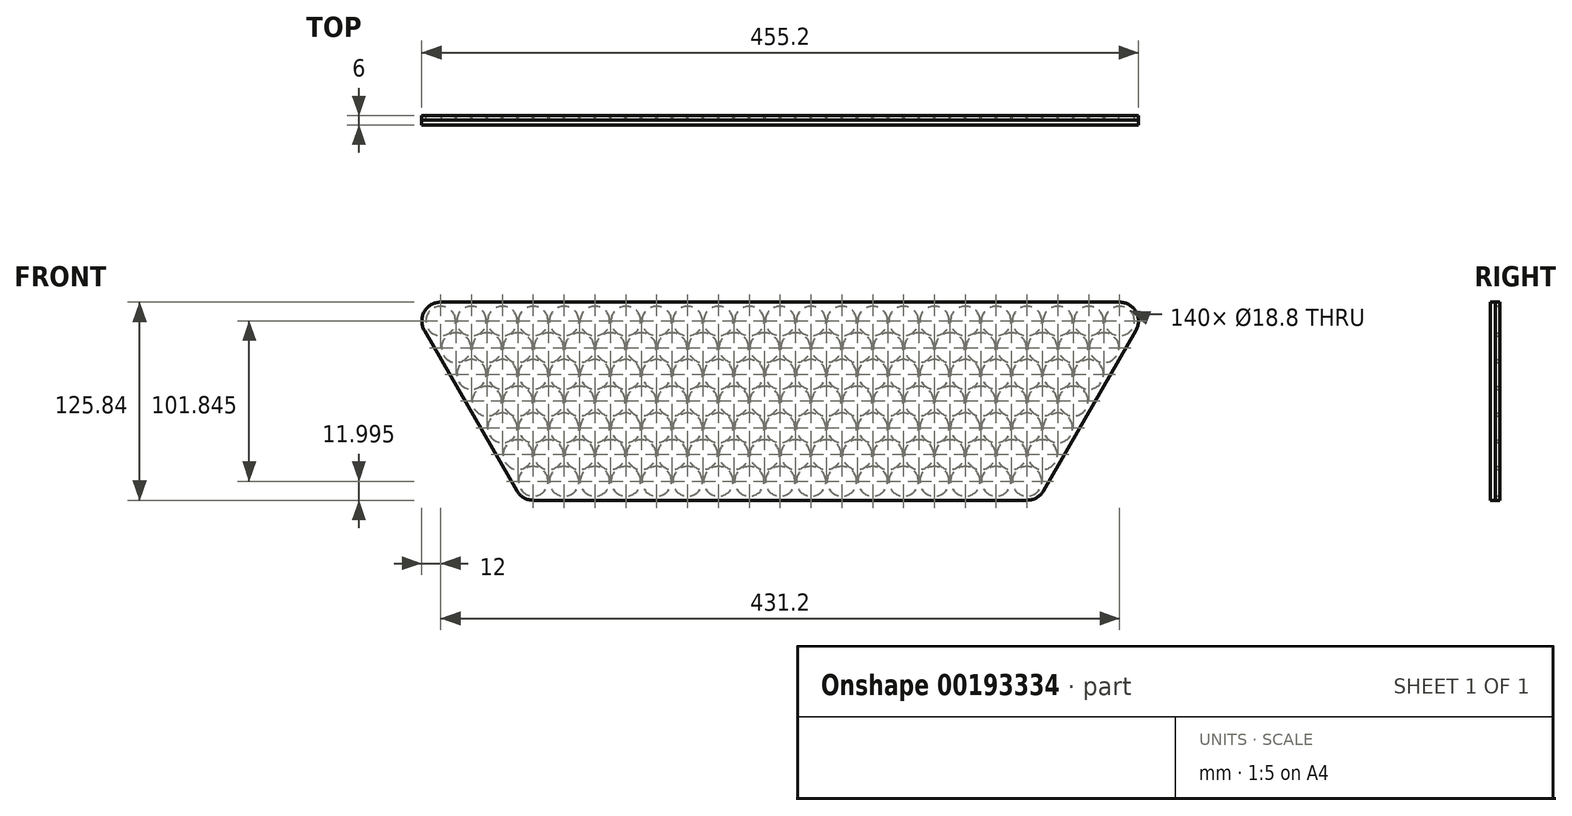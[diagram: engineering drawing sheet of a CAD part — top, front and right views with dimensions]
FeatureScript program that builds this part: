
annotation { "Feature Type Name" : "Feature", "Feature Type Description" : "" }
export const myFeature = defineFeature(function(context is Context, id is Id, definition is map)
    precondition{}
    {
        {
            var Q0;
            Q0=qCreatedBy(makeId("Front.planeOp"),FACE);
            var sketch = newSketch(context, id + "F0", { "sketchPlane" : qUnion([Q0])});
            skLineSegment(sketch, "E0", {"start": v(0, 0) * mm, "end": v(79.44, 0) * mm, "construction": true});
            skLineSegment(sketch, "E1", {"start": v(0, 0) * mm, "end": v(43.4, -75.16) * mm, "construction": true});
            skCircle(sketch, "E2", {"center": v(0, 0) * mm, "radius": 9.4 * mm});
            skCircle(sketch, "E3.1.0.0", {"center": v(19.6, 0) * mm, "radius": 9.4 * mm});
            skCircle(sketch, "E3.2.0.0", {"center": v(39.2, 0) * mm, "radius": 9.4 * mm});
            skCircle(sketch, "E3.3.0.0", {"center": v(58.8, 0) * mm, "radius": 9.4 * mm});
            skCircle(sketch, "E3.4.0.0", {"center": v(78.4, 0) * mm, "radius": 9.4 * mm});
            skCircle(sketch, "E3.5.0.0", {"center": v(98, 0) * mm, "radius": 9.4 * mm});
            skCircle(sketch, "E3.6.0.0", {"center": v(117.6, 0) * mm, "radius": 9.4 * mm});
            skCircle(sketch, "E3.7.0.0", {"center": v(137.2, 0) * mm, "radius": 9.4 * mm});
            skCircle(sketch, "E3.8.0.0", {"center": v(156.8, 0) * mm, "radius": 9.4 * mm});
            skCircle(sketch, "E3.9.0.0", {"center": v(176.4, 0) * mm, "radius": 9.4 * mm});
            skCircle(sketch, "E3.10.0.0", {"center": v(196, 0) * mm, "radius": 9.4 * mm});
            skCircle(sketch, "E3.11.0.0", {"center": v(215.6, 0) * mm, "radius": 9.4 * mm});
            skCircle(sketch, "E3.12.0.0", {"center": v(235.2, 0) * mm, "radius": 9.4 * mm});
            skCircle(sketch, "E3.13.0.0", {"center": v(254.8, 0) * mm, "radius": 9.4 * mm});
            skCircle(sketch, "E3.14.0.0", {"center": v(274.4, 0) * mm, "radius": 9.4 * mm});
            skCircle(sketch, "E3.15.0.0", {"center": v(294, 0) * mm, "radius": 9.4 * mm});
            skCircle(sketch, "E3.16.0.0", {"center": v(313.6, 0) * mm, "radius": 9.4 * mm});
            skCircle(sketch, "E3.17.0.0", {"center": v(333.2, 0) * mm, "radius": 9.4 * mm});
            skCircle(sketch, "E3.18.0.0", {"center": v(352.8, 0) * mm, "radius": 9.4 * mm});
            skCircle(sketch, "E3.19.0.0", {"center": v(372.4, 0) * mm, "radius": 9.4 * mm});
            skLineSegment(sketch, "E3.direction1", {"start": v(0, 0) * mm, "end": v(19.6, 0) * mm, "construction": true});
            skCircle(sketch, "E4.1.0.0", {"center": v(9.8, -16.97) * mm, "radius": 9.4 * mm});
            skCircle(sketch, "E4.2.0.0", {"center": v(19.6, -33.95) * mm, "radius": 9.4 * mm});
            skCircle(sketch, "E4.3.0.0", {"center": v(29.4, -50.92) * mm, "radius": 9.4 * mm});
            skCircle(sketch, "E4.4.0.0", {"center": v(39.2, -67.9) * mm, "radius": 9.4 * mm});
            skCircle(sketch, "E4.5.0.0", {"center": v(49, -84.87) * mm, "radius": 9.4 * mm});
            skCircle(sketch, "E4.6.0.0", {"center": v(58.8, -101.84) * mm, "radius": 9.4 * mm});
            skLineSegment(sketch, "E4.direction1", {"start": v(0, 0) * mm, "end": v(9.8, -16.97) * mm, "construction": true});
            skCircle(sketch, "E5.1.0.0", {"center": v(29.4, -16.97) * mm, "radius": 9.4 * mm});
            skCircle(sketch, "E5.1.0.1", {"center": v(39.2, -33.95) * mm, "radius": 9.4 * mm});
            skCircle(sketch, "E5.1.0.2", {"center": v(49, -50.92) * mm, "radius": 9.4 * mm});
            skCircle(sketch, "E5.1.0.3", {"center": v(58.8, -67.9) * mm, "radius": 9.4 * mm});
            skCircle(sketch, "E5.1.0.4", {"center": v(68.6, -84.87) * mm, "radius": 9.4 * mm});
            skCircle(sketch, "E5.1.0.5", {"center": v(78.4, -101.84) * mm, "radius": 9.4 * mm});
            skCircle(sketch, "E5.2.0.0", {"center": v(49, -16.97) * mm, "radius": 9.4 * mm});
            skCircle(sketch, "E5.2.0.1", {"center": v(58.8, -33.95) * mm, "radius": 9.4 * mm});
            skCircle(sketch, "E5.2.0.2", {"center": v(68.6, -50.92) * mm, "radius": 9.4 * mm});
            skCircle(sketch, "E5.2.0.3", {"center": v(78.4, -67.9) * mm, "radius": 9.4 * mm});
            skCircle(sketch, "E5.2.0.4", {"center": v(88.2, -84.87) * mm, "radius": 9.4 * mm});
            skCircle(sketch, "E5.2.0.5", {"center": v(98, -101.84) * mm, "radius": 9.4 * mm});
            skCircle(sketch, "E5.3.0.0", {"center": v(68.6, -16.97) * mm, "radius": 9.4 * mm});
            skCircle(sketch, "E5.3.0.1", {"center": v(78.4, -33.95) * mm, "radius": 9.4 * mm});
            skCircle(sketch, "E5.3.0.2", {"center": v(88.2, -50.92) * mm, "radius": 9.4 * mm});
            skCircle(sketch, "E5.3.0.3", {"center": v(98, -67.9) * mm, "radius": 9.4 * mm});
            skCircle(sketch, "E5.3.0.4", {"center": v(107.8, -84.87) * mm, "radius": 9.4 * mm});
            skCircle(sketch, "E5.3.0.5", {"center": v(117.6, -101.84) * mm, "radius": 9.4 * mm});
            skCircle(sketch, "E5.4.0.0", {"center": v(88.2, -16.97) * mm, "radius": 9.4 * mm});
            skCircle(sketch, "E5.4.0.1", {"center": v(98, -33.95) * mm, "radius": 9.4 * mm});
            skCircle(sketch, "E5.4.0.2", {"center": v(107.8, -50.92) * mm, "radius": 9.4 * mm});
            skCircle(sketch, "E5.4.0.3", {"center": v(117.6, -67.9) * mm, "radius": 9.4 * mm});
            skCircle(sketch, "E5.4.0.4", {"center": v(127.4, -84.87) * mm, "radius": 9.4 * mm});
            skCircle(sketch, "E5.4.0.5", {"center": v(137.2, -101.84) * mm, "radius": 9.4 * mm});
            skCircle(sketch, "E5.5.0.0", {"center": v(107.8, -16.97) * mm, "radius": 9.4 * mm});
            skCircle(sketch, "E5.5.0.1", {"center": v(117.6, -33.95) * mm, "radius": 9.4 * mm});
            skCircle(sketch, "E5.5.0.2", {"center": v(127.4, -50.92) * mm, "radius": 9.4 * mm});
            skCircle(sketch, "E5.5.0.3", {"center": v(137.2, -67.9) * mm, "radius": 9.4 * mm});
            skCircle(sketch, "E5.5.0.4", {"center": v(147, -84.87) * mm, "radius": 9.4 * mm});
            skCircle(sketch, "E5.5.0.5", {"center": v(156.8, -101.84) * mm, "radius": 9.4 * mm});
            skCircle(sketch, "E5.6.0.0", {"center": v(127.4, -16.97) * mm, "radius": 9.4 * mm});
            skCircle(sketch, "E5.6.0.1", {"center": v(137.2, -33.95) * mm, "radius": 9.4 * mm});
            skCircle(sketch, "E5.6.0.2", {"center": v(147, -50.92) * mm, "radius": 9.4 * mm});
            skCircle(sketch, "E5.6.0.3", {"center": v(156.8, -67.9) * mm, "radius": 9.4 * mm});
            skCircle(sketch, "E5.6.0.4", {"center": v(166.6, -84.87) * mm, "radius": 9.4 * mm});
            skCircle(sketch, "E5.6.0.5", {"center": v(176.4, -101.84) * mm, "radius": 9.4 * mm});
            skCircle(sketch, "E5.7.0.0", {"center": v(147, -16.97) * mm, "radius": 9.4 * mm});
            skCircle(sketch, "E5.7.0.1", {"center": v(156.8, -33.95) * mm, "radius": 9.4 * mm});
            skCircle(sketch, "E5.7.0.2", {"center": v(166.6, -50.92) * mm, "radius": 9.4 * mm});
            skCircle(sketch, "E5.7.0.3", {"center": v(176.4, -67.9) * mm, "radius": 9.4 * mm});
            skCircle(sketch, "E5.7.0.4", {"center": v(186.2, -84.87) * mm, "radius": 9.4 * mm});
            skCircle(sketch, "E5.7.0.5", {"center": v(196, -101.84) * mm, "radius": 9.4 * mm});
            skCircle(sketch, "E5.8.0.0", {"center": v(166.6, -16.97) * mm, "radius": 9.4 * mm});
            skCircle(sketch, "E5.8.0.1", {"center": v(176.4, -33.95) * mm, "radius": 9.4 * mm});
            skCircle(sketch, "E5.8.0.2", {"center": v(186.2, -50.92) * mm, "radius": 9.4 * mm});
            skCircle(sketch, "E5.8.0.3", {"center": v(196, -67.9) * mm, "radius": 9.4 * mm});
            skCircle(sketch, "E5.8.0.4", {"center": v(205.8, -84.87) * mm, "radius": 9.4 * mm});
            skCircle(sketch, "E5.8.0.5", {"center": v(215.6, -101.84) * mm, "radius": 9.4 * mm});
            skCircle(sketch, "E5.9.0.0", {"center": v(186.2, -16.97) * mm, "radius": 9.4 * mm});
            skCircle(sketch, "E5.9.0.1", {"center": v(196, -33.95) * mm, "radius": 9.4 * mm});
            skCircle(sketch, "E5.9.0.2", {"center": v(205.8, -50.92) * mm, "radius": 9.4 * mm});
            skCircle(sketch, "E5.9.0.3", {"center": v(215.6, -67.9) * mm, "radius": 9.4 * mm});
            skCircle(sketch, "E5.9.0.4", {"center": v(225.4, -84.87) * mm, "radius": 9.4 * mm});
            skCircle(sketch, "E5.9.0.5", {"center": v(235.2, -101.84) * mm, "radius": 9.4 * mm});
            skCircle(sketch, "E5.10.0.0", {"center": v(205.8, -16.97) * mm, "radius": 9.4 * mm});
            skCircle(sketch, "E5.10.0.1", {"center": v(215.6, -33.95) * mm, "radius": 9.4 * mm});
            skCircle(sketch, "E5.10.0.2", {"center": v(225.4, -50.92) * mm, "radius": 9.4 * mm});
            skCircle(sketch, "E5.10.0.3", {"center": v(235.2, -67.9) * mm, "radius": 9.4 * mm});
            skCircle(sketch, "E5.10.0.4", {"center": v(245, -84.87) * mm, "radius": 9.4 * mm});
            skCircle(sketch, "E5.10.0.5", {"center": v(254.8, -101.84) * mm, "radius": 9.4 * mm});
            skCircle(sketch, "E5.11.0.0", {"center": v(225.4, -16.97) * mm, "radius": 9.4 * mm});
            skCircle(sketch, "E5.11.0.1", {"center": v(235.2, -33.95) * mm, "radius": 9.4 * mm});
            skCircle(sketch, "E5.11.0.2", {"center": v(245, -50.92) * mm, "radius": 9.4 * mm});
            skCircle(sketch, "E5.11.0.3", {"center": v(254.8, -67.9) * mm, "radius": 9.4 * mm});
            skCircle(sketch, "E5.11.0.4", {"center": v(264.6, -84.87) * mm, "radius": 9.4 * mm});
            skCircle(sketch, "E5.11.0.5", {"center": v(274.4, -101.84) * mm, "radius": 9.4 * mm});
            skCircle(sketch, "E5.12.0.0", {"center": v(245, -16.97) * mm, "radius": 9.4 * mm});
            skCircle(sketch, "E5.12.0.1", {"center": v(254.8, -33.95) * mm, "radius": 9.4 * mm});
            skCircle(sketch, "E5.12.0.2", {"center": v(264.6, -50.92) * mm, "radius": 9.4 * mm});
            skCircle(sketch, "E5.12.0.3", {"center": v(274.4, -67.9) * mm, "radius": 9.4 * mm});
            skCircle(sketch, "E5.12.0.4", {"center": v(284.2, -84.87) * mm, "radius": 9.4 * mm});
            skCircle(sketch, "E5.12.0.5", {"center": v(294, -101.84) * mm, "radius": 9.4 * mm});
            skCircle(sketch, "E5.13.0.0", {"center": v(264.6, -16.97) * mm, "radius": 9.4 * mm});
            skCircle(sketch, "E5.13.0.1", {"center": v(274.4, -33.95) * mm, "radius": 9.4 * mm});
            skCircle(sketch, "E5.13.0.2", {"center": v(284.2, -50.92) * mm, "radius": 9.4 * mm});
            skCircle(sketch, "E5.13.0.3", {"center": v(294, -67.9) * mm, "radius": 9.4 * mm});
            skCircle(sketch, "E5.13.0.4", {"center": v(303.8, -84.87) * mm, "radius": 9.4 * mm});
            skCircle(sketch, "E5.13.0.5", {"center": v(313.6, -101.84) * mm, "radius": 9.4 * mm});
            skCircle(sketch, "E5.14.0.0", {"center": v(284.2, -16.97) * mm, "radius": 9.4 * mm});
            skCircle(sketch, "E5.14.0.1", {"center": v(294, -33.95) * mm, "radius": 9.4 * mm});
            skCircle(sketch, "E5.14.0.2", {"center": v(303.8, -50.92) * mm, "radius": 9.4 * mm});
            skCircle(sketch, "E5.14.0.3", {"center": v(313.6, -67.9) * mm, "radius": 9.4 * mm});
            skCircle(sketch, "E5.14.0.4", {"center": v(323.4, -84.87) * mm, "radius": 9.4 * mm});
            skCircle(sketch, "E5.14.0.5", {"center": v(333.2, -101.84) * mm, "radius": 9.4 * mm});
            skCircle(sketch, "E5.15.0.0", {"center": v(303.8, -16.97) * mm, "radius": 9.4 * mm});
            skCircle(sketch, "E5.15.0.1", {"center": v(313.6, -33.95) * mm, "radius": 9.4 * mm});
            skCircle(sketch, "E5.15.0.2", {"center": v(323.4, -50.92) * mm, "radius": 9.4 * mm});
            skCircle(sketch, "E5.15.0.3", {"center": v(333.2, -67.9) * mm, "radius": 9.4 * mm});
            skCircle(sketch, "E5.15.0.4", {"center": v(343, -84.87) * mm, "radius": 9.4 * mm});
            skCircle(sketch, "E5.15.0.5", {"center": v(352.8, -101.84) * mm, "radius": 9.4 * mm});
            skCircle(sketch, "E5.16.0.0", {"center": v(323.4, -16.97) * mm, "radius": 9.4 * mm});
            skCircle(sketch, "E5.16.0.1", {"center": v(333.2, -33.95) * mm, "radius": 9.4 * mm});
            skCircle(sketch, "E5.16.0.2", {"center": v(343, -50.92) * mm, "radius": 9.4 * mm});
            skCircle(sketch, "E5.16.0.3", {"center": v(352.8, -67.9) * mm, "radius": 9.4 * mm});
            skCircle(sketch, "E5.16.0.4", {"center": v(362.6, -84.87) * mm, "radius": 9.4 * mm});
            skCircle(sketch, "E5.16.0.5", {"center": v(372.4, -101.84) * mm, "radius": 9.4 * mm});
            skCircle(sketch, "E5.17.0.0", {"center": v(343, -16.97) * mm, "radius": 9.4 * mm});
            skCircle(sketch, "E5.17.0.1", {"center": v(352.8, -33.95) * mm, "radius": 9.4 * mm});
            skCircle(sketch, "E5.17.0.2", {"center": v(362.6, -50.92) * mm, "radius": 9.4 * mm});
            skCircle(sketch, "E5.17.0.3", {"center": v(372.4, -67.9) * mm, "radius": 9.4 * mm});
            skCircle(sketch, "E5.17.0.4", {"center": v(382.2, -84.87) * mm, "radius": 9.4 * mm});
            skCircle(sketch, "E5.18.0.0", {"center": v(362.6, -16.97) * mm, "radius": 9.4 * mm});
            skCircle(sketch, "E5.18.0.1", {"center": v(372.4, -33.95) * mm, "radius": 9.4 * mm});
            skCircle(sketch, "E5.18.0.2", {"center": v(382.2, -50.92) * mm, "radius": 9.4 * mm});
            skCircle(sketch, "E5.18.0.3", {"center": v(392, -67.9) * mm, "radius": 9.4 * mm});
            skCircle(sketch, "E5.19.0.0", {"center": v(382.2, -16.97) * mm, "radius": 9.4 * mm});
            skCircle(sketch, "E5.19.0.1", {"center": v(392, -33.95) * mm, "radius": 9.4 * mm});
            skCircle(sketch, "E5.19.0.2", {"center": v(401.8, -50.92) * mm, "radius": 9.4 * mm});
            skLineSegment(sketch, "E5.direction1", {"start": v(9.8, -16.97) * mm, "end": v(29.4, -16.97) * mm, "construction": true});
            skLineSegment(sketch, "E6", {"start": v(0, 0) * mm, "end": v(372.4, 0) * mm, "construction": true});
            skLineSegment(sketch, "E7", {"start": v(372.4, 0) * mm, "end": v(441, -118.82) * mm, "construction": true});
            skLineSegment(sketch, "E8", {"start": v(58.8, -101.84) * mm, "end": v(0, 0) * mm, "construction": true});
            skLineSegment(sketch, "E9", {"start": v(58.8, -101.84) * mm, "end": v(431.2, -101.84) * mm, "construction": true});
            skCircle(sketch, "E10.1.0.0", {"center": v(392, 0) * mm, "radius": 9.4 * mm});
            skCircle(sketch, "E10.2.0.0", {"center": v(411.6, 0) * mm, "radius": 9.4 * mm});
            skCircle(sketch, "E10.3.0.0", {"center": v(431.2, 0) * mm, "radius": 9.4 * mm});
            skLineSegment(sketch, "E10.direction1", {"start": v(372.4, 0) * mm, "end": v(392, 0) * mm, "construction": true});
            skCircle(sketch, "E11.1.0.0", {"center": v(401.8, -16.97) * mm, "radius": 9.4 * mm});
            skCircle(sketch, "E11.2.0.0", {"center": v(421.4, -16.97) * mm, "radius": 9.4 * mm});
            skLineSegment(sketch, "E11.direction1", {"start": v(382.2, -16.97) * mm, "end": v(401.8, -16.97) * mm, "construction": true});
            skCircle(sketch, "E12.1.0.0", {"center": v(411.6, -33.95) * mm, "radius": 9.4 * mm});
            skLineSegment(sketch, "E12.direction1", {"start": v(392, -33.95) * mm, "end": v(411.6, -33.95) * mm, "construction": true});
            skArc(sketch, "E13", {"start": v(441.6, -6) * mm, "mid": v(441.6, 6) * mm, "end": v(431.2, 12) * mm});
            skArc(sketch, "E14", {"start": v(372.4, -113.84) * mm, "mid": v(378.4, -112.24) * mm, "end": v(382.8, -107.84) * mm});
            skArc(sketch, "E15", {"start": v(0, 12) * mm, "mid": v(-10.4, 6) * mm, "end": v(-10.4, -6) * mm});
            skArc(sketch, "E16", {"start": v(48.4, -107.84) * mm, "mid": v(52.8, -112.24) * mm, "end": v(58.8, -113.84) * mm});
            skLineSegment(sketch, "E17", {"start": v(441.6, -6) * mm, "end": v(382.8, -107.84) * mm});
            skLineSegment(sketch, "E18", {"start": v(0, 12) * mm, "end": v(431.2, 12) * mm});
            skLineSegment(sketch, "E19", {"start": v(-10.4, -6) * mm, "end": v(48.4, -107.84) * mm});
            skLineSegment(sketch, "E20", {"start": v(58.8, -113.84) * mm, "end": v(372.4, -113.84) * mm});
            skSolve(sketch);
        }
        {
            var Q0;
            Q0=makeQuery(id+"F0.imprint","IMPRINT",FACE,{"disambiguationData":[TD([[makeQuery(id+"F0.imprint","IMPRINT",EDGE,{"derivedFrom":sQuery(id+"F0.wireOp",EDGE,"E2")}),-1.0]])]});
            extrude(context, id + "F1", {"entities" : qUnion([Q0]), "depth" : 3 * mm});
        }
        {
            var Q0;
            Q0=makeQuery(id+"F1.opExtrude","CAP_FACE",FACE,{"disambiguationData":[OSD([sQuery(id+"F0.wireOp",EDGE,"E2"),sQuery(id+"F0.wireOp",EDGE,"E3.1.0.0"),sQuery(id+"F0.wireOp",EDGE,"E3.2.0.0"),sQuery(id+"F0.wireOp",EDGE,"E3.3.0.0"),sQuery(id+"F0.wireOp",EDGE,"E3.4.0.0"),sQuery(id+"F0.wireOp",EDGE,"E3.5.0.0"),sQuery(id+"F0.wireOp",EDGE,"E3.6.0.0"),sQuery(id+"F0.wireOp",EDGE,"E3.7.0.0"),sQuery(id+"F0.wireOp",EDGE,"E3.8.0.0"),sQuery(id+"F0.wireOp",EDGE,"E3.9.0.0"),sQuery(id+"F0.wireOp",EDGE,"E3.10.0.0"),sQuery(id+"F0.wireOp",EDGE,"E3.11.0.0"),sQuery(id+"F0.wireOp",EDGE,"E3.12.0.0"),sQuery(id+"F0.wireOp",EDGE,"E3.13.0.0"),sQuery(id+"F0.wireOp",EDGE,"E3.14.0.0"),sQuery(id+"F0.wireOp",EDGE,"E3.15.0.0"),sQuery(id+"F0.wireOp",EDGE,"E3.16.0.0"),sQuery(id+"F0.wireOp",EDGE,"E3.17.0.0"),sQuery(id+"F0.wireOp",EDGE,"E3.18.0.0"),sQuery(id+"F0.wireOp",EDGE,"E3.19.0.0"),sQuery(id+"F0.wireOp",EDGE,"E4.1.0.0"),sQuery(id+"F0.wireOp",EDGE,"E4.2.0.0"),sQuery(id+"F0.wireOp",EDGE,"E4.3.0.0"),sQuery(id+"F0.wireOp",EDGE,"E4.4.0.0"),sQuery(id+"F0.wireOp",EDGE,"E4.5.0.0"),sQuery(id+"F0.wireOp",EDGE,"E4.6.0.0"),sQuery(id+"F0.wireOp",EDGE,"E5.1.0.0"),sQuery(id+"F0.wireOp",EDGE,"E5.1.0.1"),sQuery(id+"F0.wireOp",EDGE,"E5.1.0.2"),sQuery(id+"F0.wireOp",EDGE,"E5.1.0.3"),sQuery(id+"F0.wireOp",EDGE,"E5.1.0.4"),sQuery(id+"F0.wireOp",EDGE,"E5.1.0.5"),sQuery(id+"F0.wireOp",EDGE,"E5.2.0.0"),sQuery(id+"F0.wireOp",EDGE,"E5.2.0.1"),sQuery(id+"F0.wireOp",EDGE,"E5.2.0.2"),sQuery(id+"F0.wireOp",EDGE,"E5.2.0.3"),sQuery(id+"F0.wireOp",EDGE,"E5.2.0.4"),sQuery(id+"F0.wireOp",EDGE,"E5.2.0.5"),sQuery(id+"F0.wireOp",EDGE,"E5.3.0.0"),sQuery(id+"F0.wireOp",EDGE,"E5.3.0.1"),sQuery(id+"F0.wireOp",EDGE,"E5.3.0.2"),sQuery(id+"F0.wireOp",EDGE,"E5.3.0.3"),sQuery(id+"F0.wireOp",EDGE,"E5.3.0.4"),sQuery(id+"F0.wireOp",EDGE,"E5.3.0.5"),sQuery(id+"F0.wireOp",EDGE,"E5.4.0.0"),sQuery(id+"F0.wireOp",EDGE,"E5.4.0.1"),sQuery(id+"F0.wireOp",EDGE,"E5.4.0.2"),sQuery(id+"F0.wireOp",EDGE,"E5.4.0.3"),sQuery(id+"F0.wireOp",EDGE,"E5.4.0.4"),sQuery(id+"F0.wireOp",EDGE,"E5.4.0.5"),sQuery(id+"F0.wireOp",EDGE,"E5.5.0.0"),sQuery(id+"F0.wireOp",EDGE,"E5.5.0.1"),sQuery(id+"F0.wireOp",EDGE,"E5.5.0.2"),sQuery(id+"F0.wireOp",EDGE,"E5.5.0.3"),sQuery(id+"F0.wireOp",EDGE,"E5.5.0.4"),sQuery(id+"F0.wireOp",EDGE,"E5.5.0.5"),sQuery(id+"F0.wireOp",EDGE,"E5.6.0.0"),sQuery(id+"F0.wireOp",EDGE,"E5.6.0.1"),sQuery(id+"F0.wireOp",EDGE,"E5.6.0.2"),sQuery(id+"F0.wireOp",EDGE,"E5.6.0.3"),sQuery(id+"F0.wireOp",EDGE,"E5.6.0.4"),sQuery(id+"F0.wireOp",EDGE,"E5.6.0.5"),sQuery(id+"F0.wireOp",EDGE,"E5.7.0.0"),sQuery(id+"F0.wireOp",EDGE,"E5.7.0.1"),sQuery(id+"F0.wireOp",EDGE,"E5.7.0.2"),sQuery(id+"F0.wireOp",EDGE,"E5.7.0.3"),sQuery(id+"F0.wireOp",EDGE,"E5.7.0.4"),sQuery(id+"F0.wireOp",EDGE,"E5.7.0.5"),sQuery(id+"F0.wireOp",EDGE,"E5.8.0.0"),sQuery(id+"F0.wireOp",EDGE,"E5.8.0.1"),sQuery(id+"F0.wireOp",EDGE,"E5.8.0.2"),sQuery(id+"F0.wireOp",EDGE,"E5.8.0.3"),sQuery(id+"F0.wireOp",EDGE,"E5.8.0.4"),sQuery(id+"F0.wireOp",EDGE,"E5.8.0.5"),sQuery(id+"F0.wireOp",EDGE,"E5.9.0.0"),sQuery(id+"F0.wireOp",EDGE,"E5.9.0.1"),sQuery(id+"F0.wireOp",EDGE,"E5.9.0.2"),sQuery(id+"F0.wireOp",EDGE,"E5.9.0.3"),sQuery(id+"F0.wireOp",EDGE,"E5.9.0.4"),sQuery(id+"F0.wireOp",EDGE,"E5.9.0.5"),sQuery(id+"F0.wireOp",EDGE,"E5.10.0.0"),sQuery(id+"F0.wireOp",EDGE,"E5.10.0.1"),sQuery(id+"F0.wireOp",EDGE,"E5.10.0.2"),sQuery(id+"F0.wireOp",EDGE,"E5.10.0.3"),sQuery(id+"F0.wireOp",EDGE,"E5.10.0.4"),sQuery(id+"F0.wireOp",EDGE,"E5.10.0.5"),sQuery(id+"F0.wireOp",EDGE,"E5.11.0.0"),sQuery(id+"F0.wireOp",EDGE,"E5.11.0.1"),sQuery(id+"F0.wireOp",EDGE,"E5.11.0.2"),sQuery(id+"F0.wireOp",EDGE,"E5.11.0.3"),sQuery(id+"F0.wireOp",EDGE,"E5.11.0.4"),sQuery(id+"F0.wireOp",EDGE,"E5.11.0.5"),sQuery(id+"F0.wireOp",EDGE,"E5.12.0.0"),sQuery(id+"F0.wireOp",EDGE,"E5.12.0.1"),sQuery(id+"F0.wireOp",EDGE,"E5.12.0.2"),sQuery(id+"F0.wireOp",EDGE,"E5.12.0.3"),sQuery(id+"F0.wireOp",EDGE,"E5.12.0.4"),sQuery(id+"F0.wireOp",EDGE,"E5.12.0.5"),sQuery(id+"F0.wireOp",EDGE,"E5.13.0.0"),sQuery(id+"F0.wireOp",EDGE,"E5.13.0.1"),sQuery(id+"F0.wireOp",EDGE,"E5.13.0.2"),sQuery(id+"F0.wireOp",EDGE,"E5.13.0.3"),sQuery(id+"F0.wireOp",EDGE,"E5.13.0.4"),sQuery(id+"F0.wireOp",EDGE,"E5.13.0.5"),sQuery(id+"F0.wireOp",EDGE,"E5.14.0.0"),sQuery(id+"F0.wireOp",EDGE,"E5.14.0.1"),sQuery(id+"F0.wireOp",EDGE,"E5.14.0.2"),sQuery(id+"F0.wireOp",EDGE,"E5.14.0.3"),sQuery(id+"F0.wireOp",EDGE,"E5.14.0.4"),sQuery(id+"F0.wireOp",EDGE,"E5.14.0.5"),sQuery(id+"F0.wireOp",EDGE,"E5.15.0.0"),sQuery(id+"F0.wireOp",EDGE,"E5.15.0.1"),sQuery(id+"F0.wireOp",EDGE,"E5.15.0.2"),sQuery(id+"F0.wireOp",EDGE,"E5.15.0.3"),sQuery(id+"F0.wireOp",EDGE,"E5.15.0.4"),sQuery(id+"F0.wireOp",EDGE,"E5.15.0.5"),sQuery(id+"F0.wireOp",EDGE,"E5.16.0.0"),sQuery(id+"F0.wireOp",EDGE,"E5.16.0.1"),sQuery(id+"F0.wireOp",EDGE,"E5.16.0.2"),sQuery(id+"F0.wireOp",EDGE,"E5.16.0.3"),sQuery(id+"F0.wireOp",EDGE,"E5.16.0.4"),sQuery(id+"F0.wireOp",EDGE,"E5.16.0.5"),sQuery(id+"F0.wireOp",EDGE,"E5.17.0.0"),sQuery(id+"F0.wireOp",EDGE,"E5.17.0.1"),sQuery(id+"F0.wireOp",EDGE,"E5.17.0.2"),sQuery(id+"F0.wireOp",EDGE,"E5.17.0.3"),sQuery(id+"F0.wireOp",EDGE,"E5.17.0.4"),sQuery(id+"F0.wireOp",EDGE,"E5.18.0.0"),sQuery(id+"F0.wireOp",EDGE,"E5.18.0.1"),sQuery(id+"F0.wireOp",EDGE,"E5.18.0.2"),sQuery(id+"F0.wireOp",EDGE,"E5.18.0.3"),sQuery(id+"F0.wireOp",EDGE,"E5.19.0.0"),sQuery(id+"F0.wireOp",EDGE,"E5.19.0.1"),sQuery(id+"F0.wireOp",EDGE,"E5.19.0.2"),sQuery(id+"F0.wireOp",EDGE,"E10.1.0.0"),sQuery(id+"F0.wireOp",EDGE,"E10.2.0.0"),sQuery(id+"F0.wireOp",EDGE,"E10.3.0.0"),sQuery(id+"F0.wireOp",EDGE,"E11.1.0.0"),sQuery(id+"F0.wireOp",EDGE,"E11.2.0.0"),sQuery(id+"F0.wireOp",EDGE,"E12.1.0.0"),sQuery(id+"F0.wireOp",EDGE,"E13"),sQuery(id+"F0.wireOp",EDGE,"E14"),sQuery(id+"F0.wireOp",EDGE,"E15"),sQuery(id+"F0.wireOp",EDGE,"E16"),sQuery(id+"F0.wireOp",EDGE,"E17"),sQuery(id+"F0.wireOp",EDGE,"E18"),sQuery(id+"F0.wireOp",EDGE,"E19"),sQuery(id+"F0.wireOp",EDGE,"E20")])],"isStart":false});
            var sketch = newSketch(context, id + "F2", { "sketchPlane" : qUnion([Q0])});
            skArc(sketch, "E21.0", {"start": v(0, 12) * mm, "mid": v(-10.4, 6) * mm, "end": v(-10.4, -6) * mm});
            skLineSegment(sketch, "E21.1", {"start": v(0, 12) * mm, "end": v(431.2, 12) * mm});
            skLineSegment(sketch, "E21.2", {"start": v(-10.4, -6) * mm, "end": v(48.4, -107.84) * mm});
            skArc(sketch, "E21.3", {"start": v(48.4, -107.84) * mm, "mid": v(52.8, -112.24) * mm, "end": v(58.8, -113.84) * mm});
            skLineSegment(sketch, "E21.4", {"start": v(58.8, -113.84) * mm, "end": v(372.4, -113.84) * mm});
            skArc(sketch, "E21.5", {"start": v(441.6, -6) * mm, "mid": v(441.6, 6) * mm, "end": v(431.2, 12) * mm});
            skLineSegment(sketch, "E21.6", {"start": v(441.6, -6) * mm, "end": v(382.8, -107.84) * mm});
            skArc(sketch, "E21.7", {"start": v(372.4, -113.84) * mm, "mid": v(378.4, -112.24) * mm, "end": v(382.8, -107.84) * mm});
            skSolve(sketch);
        }
        {
            var Q0;
            Q0=qSketchRegion(id+"F2",true);
            extrude(context, id + "F3", {"entities" : qUnion([Q0]), "depth" : 3 * mm});
        }
    });
